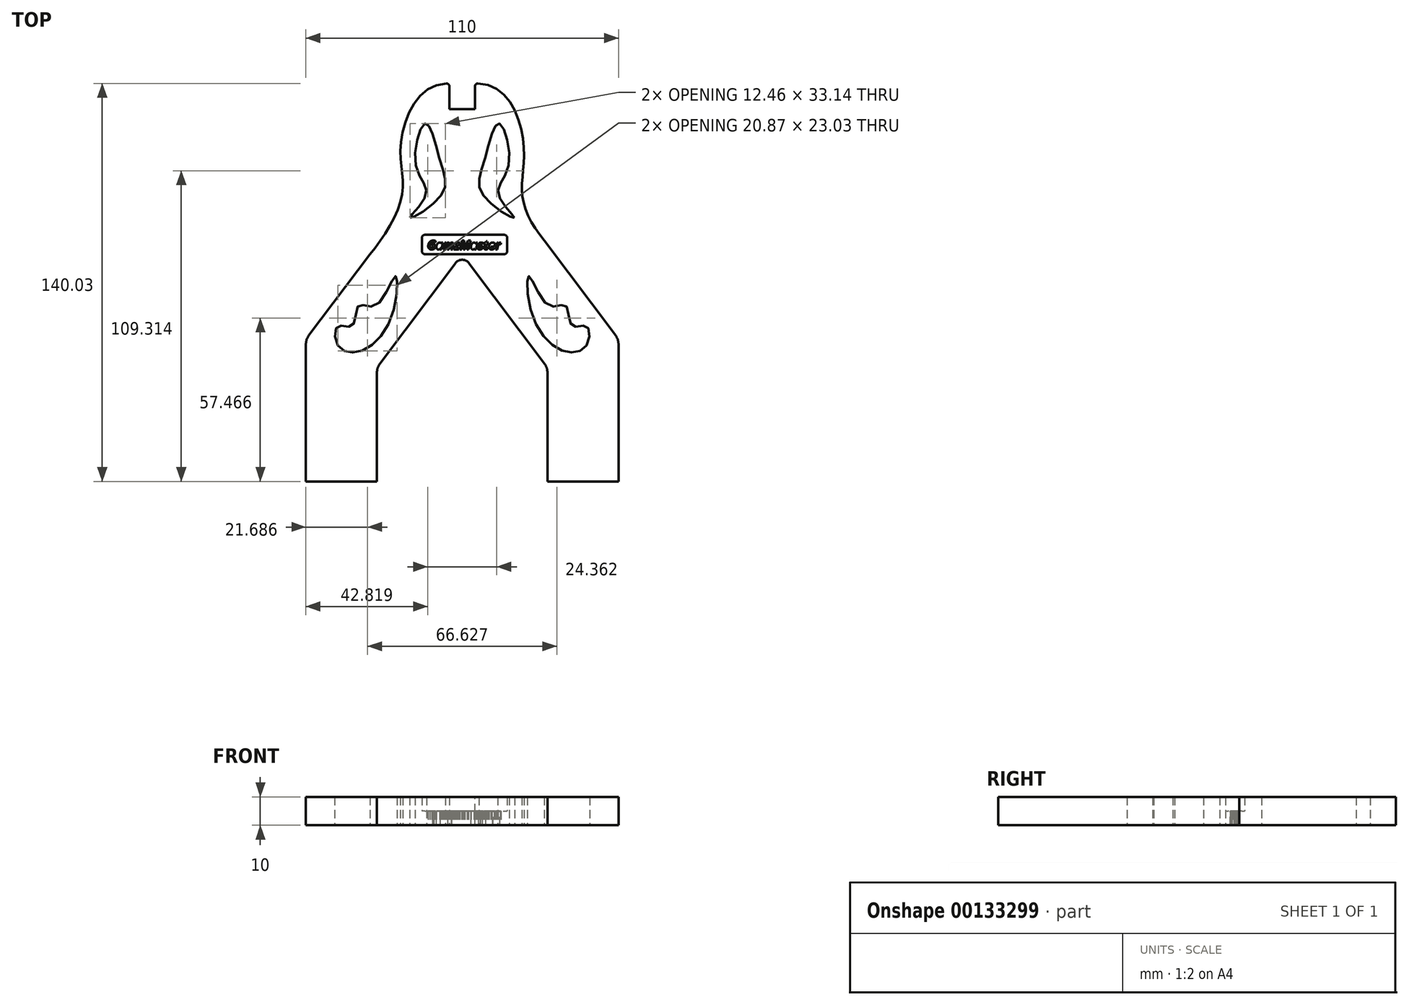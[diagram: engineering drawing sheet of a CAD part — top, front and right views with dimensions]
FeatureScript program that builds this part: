
annotation { "Feature Type Name" : "Feature", "Feature Type Description" : "" }
export const myFeature = defineFeature(function(context is Context, id is Id, definition is map)
    precondition{}
    {
        {
            var Q0;
            Q0=qCreatedBy(makeId("Top.planeOp"),FACE);
            var sketch = newSketch(context, id + "F0", { "sketchPlane" : qUnion([Q0])});
            skLineSegment(sketch, "E0", {"start": v(-52, -80) * mm, "end": v(-33, -80) * mm});
            skLineSegment(sketch, "E1", {"start": v(-55, -77) * mm, "end": v(-55, -40) * mm});
            skLineSegment(sketch, "E2", {"start": v(-30, -77) * mm, "end": v(-30, -40) * mm});
            skLineSegment(sketch, "E3.MirrorCS", {"start": v(30, -77) * mm, "end": v(30, -40) * mm});
            skLineSegment(sketch, "E4.MirrorCS", {"start": v(55, -76.67) * mm, "end": v(55, -40) * mm});
            skLineSegment(sketch, "E5.MirrorCS", {"start": v(52.37, -80) * mm, "end": v(33, -80) * mm});
            skLineSegment(sketch, "E6", {"start": v(-30, -40) * mm, "end": v(-2.4, -3.2) * mm});
            skLineSegment(sketch, "E7", {"start": v(2.4, -3.2) * mm, "end": v(30, -40) * mm});
            skLineSegment(sketch, "E8", {"start": v(-55, -40) * mm, "end": v(-55, -30) * mm});
            skLineSegment(sketch, "E9.MirrorCS", {"start": v(55, -40) * mm, "end": v(55, -30) * mm});
            skLineSegment(sketch, "E10", {"start": v(-55, -30) * mm, "end": v(-32.5, 0) * mm});
            skLineSegment(sketch, "E11.MirrorCS", {"start": v(55, -30) * mm, "end": v(28.87, 4.84) * mm});
            skLineSegment(sketch, "E12", {"start": v(-4.5, 60) * mm, "end": v(-4.5, 55.5) * mm});
            skLineSegment(sketch, "E13", {"start": v(-1.5, 51) * mm, "end": v(1.5, 51) * mm});
            skLineSegment(sketch, "E14", {"start": v(4.5, 55.5) * mm, "end": v(4.5, 60) * mm});
            skFitSpline(sketch, "E15", {"points": [v(-32.5, 0) * mm, v(-21.14, 20.78) * mm, v(-21.61, 38.68) * mm, v(-4.5, 60) * mm], "startDerivative": vector(40.27, 47.4) * mm, "endDerivative": vector(92, -5.37) * mm});
            skFitSpline(sketch, "E16.MirrorCS", {"points": [v(28.87, 4.84) * mm, v(21.14, 20.78) * mm, v(21.61, 38.68) * mm, v(4.5, 60) * mm], "startDerivative": vector(-40.27, 47.4) * mm, "endDerivative": vector(-92, -5.37) * mm});
            skPoint(sketch, "E17.visualSharp", {"position": v(0, 0) * mm});
            skArc(sketch, "E17.filletArc", {"start": v(2.4, -3.2) * mm, "mid": v(0, -2) * mm, "end": v(-2.4, -3.2) * mm});
            skFitSpline(sketch, "E18", {"points": [v(-18.4, 12.75) * mm, v(-12.74, 20.76) * mm, v(-16.26, 30.92) * mm, v(-12.94, 45.97) * mm, v(-7.66, 32.48) * mm, v(-7.47, 20.56) * mm, v(-18.4, 12.75) * mm]});
            skFitSpline(sketch, "E19.MirrorC", {"points": [v(18.4, 12.75) * mm, v(12.74, 20.76) * mm, v(16.26, 30.92) * mm, v(12.94, 45.97) * mm, v(7.66, 32.48) * mm, v(7.47, 20.56) * mm, v(18.4, 12.75) * mm]});
            skLineSegment(sketch, "E20", {"start": v(-55, -77) * mm, "end": v(-55, -80) * mm});
            skLineSegment(sketch, "E21", {"start": v(-55, -80) * mm, "end": v(-52, -80) * mm});
            skLineSegment(sketch, "E22", {"start": v(-30, -77) * mm, "end": v(-30, -80) * mm});
            skLineSegment(sketch, "E23", {"start": v(-30, -80) * mm, "end": v(-33, -80) * mm});
            skLineSegment(sketch, "E24", {"start": v(30, -77) * mm, "end": v(30, -80) * mm});
            skLineSegment(sketch, "E25", {"start": v(30, -80) * mm, "end": v(33, -80) * mm});
            skLineSegment(sketch, "E26", {"start": v(55, -76.67) * mm, "end": v(55, -80) * mm});
            skLineSegment(sketch, "E27", {"start": v(55, -80) * mm, "end": v(52.37, -80) * mm});
            skLineSegment(sketch, "E28", {"start": v(-4.5, 55.5) * mm, "end": v(-4.5, 51) * mm});
            skLineSegment(sketch, "E29", {"start": v(-4.5, 51) * mm, "end": v(-1.5, 51) * mm});
            skLineSegment(sketch, "E30", {"start": v(4.5, 55.5) * mm, "end": v(4.5, 51) * mm});
            skLineSegment(sketch, "E31", {"start": v(4.5, 51) * mm, "end": v(1.5, 51) * mm});
            skPoint(sketch, "E32.0.internal.snap0", {"position": v(-43.75, -15) * mm});
            skPoint(sketch, "E32.7.internal.snap0", {"position": v(-43.75, -15) * mm});
            skFitSpline(sketch, "E32", {"points": [v(-43.75, -32.11) * mm, v(-36.3, -34.3) * mm, v(-24.86, -21.94) * mm, v(-23.59, -7.77) * mm, v(-30.5, -18.12) * mm, v(-36.49, -18.12) * mm, v(-38.67, -25.2) * mm, v(-43.75, -25.4) * mm, v(-43.75, -32.11) * mm]});
            skLineSegment(sketch, "E33", {"start": v(0, 0) * mm, "end": v(0, -80) * mm, "construction": true});
            skFitSpline(sketch, "E34.MirrorC", {"points": [v(43.75, -32.11) * mm, v(36.3, -34.3) * mm, v(24.86, -21.94) * mm, v(23.59, -7.77) * mm, v(30.5, -18.12) * mm, v(36.49, -18.12) * mm, v(38.67, -25.2) * mm, v(43.75, -25.4) * mm, v(43.75, -32.11) * mm]});
            skLineSegment(sketch, "E35", {"start": v(36.5, 0) * mm, "end": v(-36.46, 0) * mm, "construction": true});
            skText(sketch, "E36", { "text": "GamzMaster", "fontName": "OpenSans-BoldItalic.ttf"});
            skLineSegment(sketch, "E37.bottom", {"start": v(-14.15, 6.76) * mm, "end": v(15.85, 6.76) * mm});
            skLineSegment(sketch, "E37.top", {"start": v(-14.15, 0) * mm, "end": v(15.85, 0) * mm});
            skLineSegment(sketch, "E37.left", {"start": v(-14.15, 6.76) * mm, "end": v(-14.15, 0) * mm});
            skLineSegment(sketch, "E37.right", {"start": v(15.85, 6.76) * mm, "end": v(15.85, 0) * mm});
            const initialGuessF0  = {"E36": [-0.01222, 0.00167, 1, 0, 0.00309]};
            skSetInitialGuess(sketch, initialGuessF0);
            skSolve(sketch);
        }
        {
            var Q0;
            Q0=makeQuery(id+"F0.imprint","IMPRINT",FACE,{"disambiguationData":[TD([[makeQuery(id+"F0.imprint","IMPRINT",EDGE,{"derivedFrom":sQuery(id+"F0.wireOp",EDGE,"E0")}),1.0]])]});
            extrude(context, id + "F1", {"entities" : qUnion([Q0]), "depth" : 10 * mm});
        }
        {
            var Q0;
            Q0=makeQuery(id+"F1.opExtrude","SWEPT_EDGE",EDGE,{"disambiguationData":[OSD([sQuery(id+"F0.wireOp",EDGE,"E8"),sQuery(id+"F0.wireOp",EDGE,"E10")])]});
            fillet(context, id + "F2", {"entities" : qUnion([Q0]), "radius" : 5 * mm, "tangentPropagation" : true, "allowEdgeOverflow" : false});
        }
        {
            var Q0;
            Q0=makeQuery(id+"F1.opExtrude","SWEPT_EDGE",EDGE,{"disambiguationData":[OSD([sQuery(id+"F0.wireOp",EDGE,"E9.MirrorCS"),sQuery(id+"F0.wireOp",EDGE,"E11.MirrorCS")])]});
            fillet(context, id + "F3", {"entities" : qUnion([Q0]), "radius" : 5 * mm, "tangentPropagation" : true, "allowEdgeOverflow" : false});
        }
        {
            var Q0;
            Q0=makeQuery(id+"F1.opExtrude","SWEPT_EDGE",EDGE,{"disambiguationData":[OSD([sQuery(id+"F0.wireOp",EDGE,"E2"),sQuery(id+"F0.wireOp",EDGE,"E6")])]});
            fillet(context, id + "F4", {"entities" : qUnion([Q0]), "radius" : 5 * mm, "tangentPropagation" : true, "allowEdgeOverflow" : false});
        }
        {
            var Q0;
            Q0=makeQuery(id+"F1.opExtrude","SWEPT_EDGE",EDGE,{"disambiguationData":[OSD([sQuery(id+"F0.wireOp",EDGE,"E3.MirrorCS"),sQuery(id+"F0.wireOp",EDGE,"E7")])]});
            fillet(context, id + "F5", {"entities" : qUnion([Q0]), "radius" : 5 * mm, "tangentPropagation" : true, "allowEdgeOverflow" : false});
        }
        {
            var Q0;
            Q0=makeQuery(id+"F1.opExtrude","SWEPT_EDGE",EDGE,{"disambiguationData":[OSD([sQuery(id+"F0.wireOp",EDGE,"E12"),sQuery(id+"F0.wireOp",EDGE,"E15")])]});
            var Q1;
            Q1=makeQuery(id+"F1.opExtrude","SWEPT_EDGE",EDGE,{"disambiguationData":[OSD([sQuery(id+"F0.wireOp",EDGE,"E14"),sQuery(id+"F0.wireOp",EDGE,"E16.MirrorCS")])]});
            fillet(context, id + "F6", {"entities" : qUnion([Q0, Q1]), "radius" : 1 * mm, "tangentPropagation" : true, "allowEdgeOverflow" : false});
        }
        {
            var Q0;
            Q0=makeQuery(id+"F0.imprint","IMPRINT",FACE,{"disambiguationData":[TD([[makeQuery(id+"F0.imprint","IMPRINT",EDGE,{"derivedFrom":sQuery(id+"F0.wireOp",EDGE,"E36.sketch_text.stroke-0")}),1.0]])]});
            extrude(context, id + "F7", {"entities" : qUnion([Q0]), "operationType" : NewBodyOperationType.ADD, "depth" : 5 * mm});
        }
        {
            var Q0;
            Q0=makeQuery(id+"F1.opExtrude","SWEPT_EDGE",EDGE,{"disambiguationData":[OSD([sQuery(id+"F0.wireOp",EDGE,"E37.bottom"),sQuery(id+"F0.wireOp",EDGE,"E37.left")])]});
            var Q1;
            Q1=makeQuery(id+"F1.opExtrude","SWEPT_EDGE",EDGE,{"disambiguationData":[OSD([sQuery(id+"F0.wireOp",EDGE,"E37.bottom"),sQuery(id+"F0.wireOp",EDGE,"E37.right")])]});
            var Q2;
            Q2=makeQuery(id+"F1.opExtrude","SWEPT_EDGE",EDGE,{"disambiguationData":[OSD([sQuery(id+"F0.wireOp",EDGE,"E37.top"),sQuery(id+"F0.wireOp",EDGE,"E37.left")])]});
            var Q3;
            Q3=makeQuery(id+"F1.opExtrude","SWEPT_EDGE",EDGE,{"disambiguationData":[OSD([sQuery(id+"F0.wireOp",EDGE,"E37.top"),sQuery(id+"F0.wireOp",EDGE,"E37.right")])]});
            fillet(context, id + "F8", {"entities" : qUnion([Q0, Q1, Q2, Q3]), "radius" : 1 * mm, "tangentPropagation" : true, "allowEdgeOverflow" : false});
        }
    });
